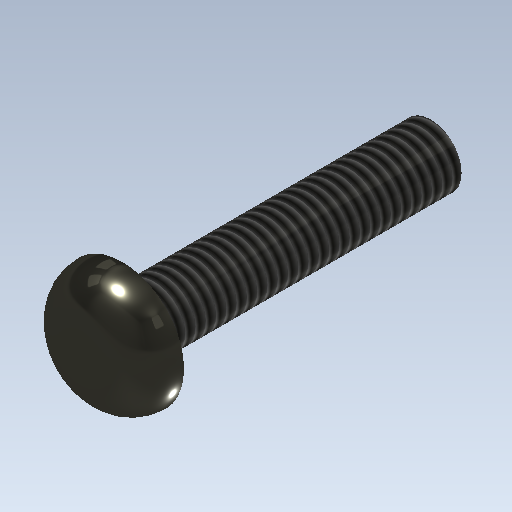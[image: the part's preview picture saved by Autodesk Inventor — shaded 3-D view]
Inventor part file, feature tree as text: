
AUTODESK INVENTOR PART (.ipt)
format: ipt  version: 2020.2 (Build 242310000, 310)  size: 172,544 bytes
history: native  units: mm
features: extrude x3, sketch x3, other x1, fillet x1, thread x1
ambient origin geometry x1: Origin
bodies: Body1 (feature_tree)
feature tree (9):
  other  "ソリッド1"
  extrude  "押し出し1"  Depth=3.0mm
  extrude  "押し出し2"  Depth=6.0mm TaperAngle=0.0deg
  fillet  "フィレット1"  Radius=6.0mm
  thread  "ねじ1"
  extrude  "押し出し3"  Depth=2.0mm TaperAngle=0.0deg
  sketch  "スケッチ1"
  sketch  "スケッチ2"
  sketch  "スケッチ3"
